# Revit family: QF_BOURGEAT_bain_marie_couvercle_standard_modulo
name_source: partatom
category: Equipement spécialisé
revit_build: Autodesk Revit 2015 (Build: 20140606_1530(x64)
units: mm (PartAtom-declared; Revit-internal decimal feet)

## types (2) — shared parameters
Charge max = 10.00 kg
Fabricant = BOURGEAT
Fréquence = 50 Hz
Hauteur hors tout = 250 mm  [stored 0.82021 ft]
Indice de protection = 54
Intensité nominale = 3 A
Phase = 2
Poids net à vide = 7.00 kg
Puissance électrique  = 700 W
Spécification du Fabricant = bain_marie_modulo
Tension = 230 V
URL catalogue = http://www.bourgeat.fr
support = Oui

## per-type parameters (varying)
| type | Longueur hors tout | Modèle | Profondeur hors tout |
| bain_marie | 545 mm  [stored 1.78806 ft] | 875005 | 345 mm  [stored 1.13189 ft] |
| bain_marie+support | 620 mm  [stored 2.03412 ft] | 875005+875000 | 350 mm  [stored 1.14829 ft] |

note: [stored X ft] marks values corroborated as IEEE doubles in the binary element streams (Revit-internal decimal feet)
